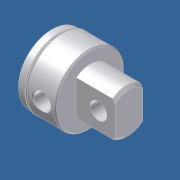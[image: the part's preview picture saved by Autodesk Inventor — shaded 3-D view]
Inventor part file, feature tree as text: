
AUTODESK INVENTOR PART (.ipt)
format: ipt  version: unknown  size: 314,368 bytes
history: native  units: in
note: dims shown in document units (in); Inventor stores cm internally (conversion verified against a paired STEP export)
features: other x126, sketch x8, revolve x6, extrude x2
ambient origin geometry x8: Origin, YZ Plane, XZ Plane, XY Plane, X Axis, Y Axis, Z Axis, Center Point
feature tree (142):
  revolve  "Revolution1"  Angle=360.0deg
  revolve  "Revolution2"  Angle=360.0deg
  extrude  "Extrusion1"  TaperAngle=360.0deg  [1 undecoded]
  revolve  "Revolution3"  [1 undecoded]
  revolve  "Revolution4"  [1 undecoded]
  revolve  "Revolution5"  [1 undecoded]
  revolve  "Revolution6"  [1 undecoded]
  extrude  "Extrusion2"  [1 undecoded]
  other  "f_XY"
  other  "f_YZ"
  other  "f_ZX"
  other  "f_X"
  other  "f_Y"
  other  "f_Z"
  other  "f_Center"
  other  "lovra1_XY"
  other  "lovra1_YZ"
  other  "lovra1_ZX"
  other  "lovra1_X"
  other  "lovra1_Y"
  other  "lovra1_Z"
  other  "lovra1_Center"
  other  "lovra2_XY"
  other  "lovra2_YZ"
  other  "lovra2_ZX"
  other  "lovra2_X"
  other  "lovra2_Y"
  other  "lovra2_Z"
  other  "lovra2_Center"
  other  "lovra21_XY"
  other  "lovra21_YZ"
  other  "lovra21_ZX"
  other  "lovra21_X"
  other  "lovra21_Y"
  other  "lovra21_Z"
  other  "lovra21_Center"
  other  "lovra22_XY"
  other  "lovra22_YZ"
  other  "lovra22_ZX"
  other  "lovra22_X"
  other  "lovra22_Y"
  other  "lovra22_Z"
  other  "lovra22_Center"
  other  "lovra3_XY"
  other  "lovra3_YZ"
  other  "lovra3_ZX"
  other  "lovra3_X"
  other  "lovra3_Y"
  other  "lovra3_Z"
  other  "lovra3_Center"
  other  "olen_XY"
  other  "olen_YZ"
  other  "olen_ZX"
  other  "olen_X"
  other  "olen_Y"
  other  "olen_Z"
  other  "olen_Center"
  other  "p1_XY"
  other  "p1_YZ"
  other  "p1_ZX"
  other  "p1_X"
  other  "p1_Y"
  other  "p1_Z"
  other  "p1_Center"
  other  "p2_XY"
  other  "p2_YZ"
  other  "p2_ZX"
  other  "p2_X"
  other  "p2_Y"
  other  "p2_Z"
  other  "p2_Center"
  other  "port_XY"
  other  "port_YZ"
  other  "port_ZX"
  other  "port_X"
  other  "port_Y"
  other  "port_Z"
  other  "port_Center"
  other  "port2_XY"
  other  "port2_YZ"
  other  "port2_ZX"
  other  "port2_X"
  other  "port2_Y"
  other  "port2_Z"
  other  "port2_Center"
  other  "thd1_XY"
  other  "thd1_YZ"
  other  "thd1_ZX"
  other  "thd1_X"
  other  "thd1_Y"
  other  "thd1_Z"
  other  "thd1_Center"
  other  "thd2_XY"
  other  "thd2_YZ"
  other  "thd2_ZX"
  other  "thd2_X"
  other  "thd2_Y"
  other  "thd2_Z"
  other  "thd2_Center"
  other  "to_mounting_bracket_XY"
  other  "to_mounting_bracket_YZ"
  other  "to_mounting_bracket_ZX"
  other  "to_mounting_bracket_X"
  other  "to_mounting_bracket_Y"
  other  "to_mounting_bracket_Z"
  other  "to_mounting_bracket_Center"
  other  "to_nut_XY"
  other  "to_nut_YZ"
  other  "to_nut_ZX"
  other  "to_nut_X"
  other  "to_nut_Y"
  other  "to_nut_Z"
  other  "to_nut_Center"
  other  "to_pin_XY"
  other  "to_pin_YZ"
  other  "to_pin_ZX"
  other  "to_pin_X"
  other  "to_pin_Y"
  other  "to_pin_Z"
  other  "to_pin_Center"
  other  "to_screw_XY"
  other  "to_screw_YZ"
  other  "to_screw_ZX"
  other  "to_screw_X"
  other  "to_screw_Y"
  other  "to_screw_Z"
  other  "to_screw_Center"
  other  "to_tube_XY"
  other  "to_tube_YZ"
  other  "to_tube_ZX"
  other  "to_tube_X"
  other  "to_tube_Y"
  other  "to_tube_Z"
  other  "to_tube_Center"
  sketch  "Sketch_18"  dims[d5=360.0deg d6=360.0deg]
  sketch  "Sketch_21"
  sketch  "Sketch_9"  dims[d0=360.0deg d1=360.0deg]
  sketch  "Sketch_13"  dims[d2=0.875in d3=0.0in d4=360.0deg]
  sketch  "Sketch_19"  dims[d7=360.0deg d8=0.9255in d9=0.0in]
  sketch  "Sketch_20"
  sketch  "Sketch_24"
  sketch  "Sketch_43"
note: 6 required parameter values undecoded (feature->parameter linkage not recoverable at this tier; creation-order binding heuristic only, values carry confidence <= 0.55)